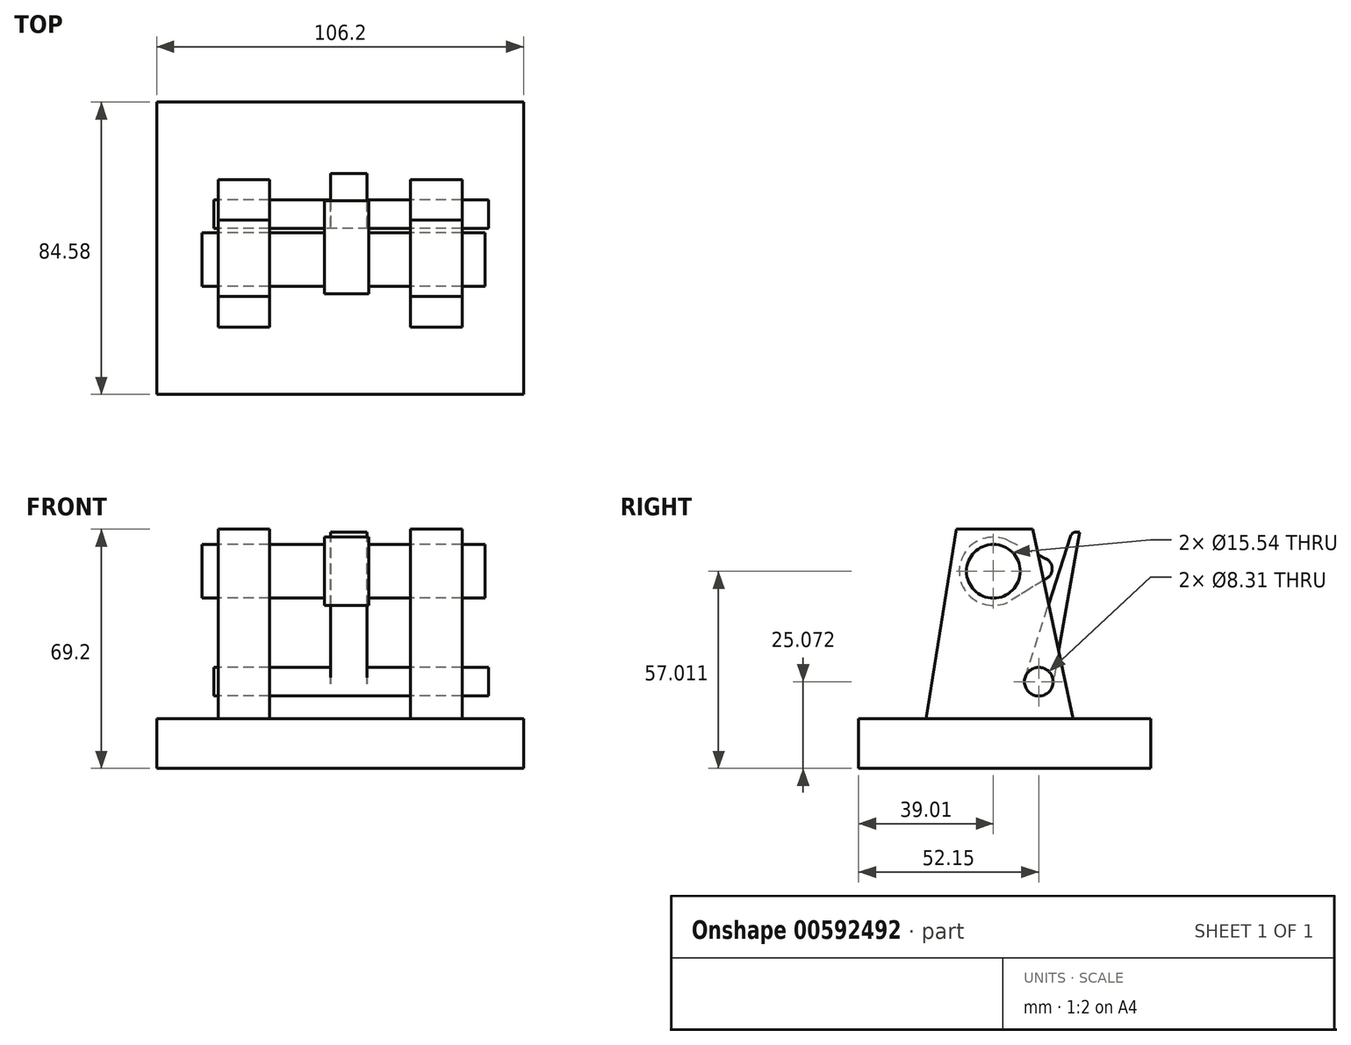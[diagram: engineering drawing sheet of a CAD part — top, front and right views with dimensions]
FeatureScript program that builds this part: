
annotation { "Feature Type Name" : "Feature", "Feature Type Description" : "" }
export const myFeature = defineFeature(function(context is Context, id is Id, definition is map)
    precondition{}
    {
        {
            var Q0;
            Q0=qCreatedBy(makeId("Right.planeOp"),FACE);
            var sketch = newSketch(context, id + "F0", { "sketchPlane" : qUnion([Q0])});
            skLineSegment(sketch, "E0.bottom", {"start": v(-39, 0) * mm, "end": v(45.57, 0) * mm});
            skLineSegment(sketch, "E0.top", {"start": v(-39, -14.35) * mm, "end": v(45.57, -14.35) * mm});
            skLineSegment(sketch, "E0.left", {"start": v(-39, 0) * mm, "end": v(-39, -14.35) * mm});
            skLineSegment(sketch, "E0.right", {"start": v(45.57, 0) * mm, "end": v(45.57, -14.35) * mm});
            skSolve(sketch);
        }
        {
            var Q0;
            Q0 = qSketchRegion(id + "F0", true);
            extrude(context, id + "F1", {"entities" : qUnion([Q0]), "endBound" : BoundingType.SYMMETRIC, "depth" : 106.2 * mm, "offsetDistance" : 25 * mm});
        }
        {
            var Q0;
            Q0=qCreatedBy(makeId("Right.planeOp"),FACE);
            var sketch = newSketch(context, id + "F2", { "sketchPlane" : qUnion([Q0])});
            skLineSegment(sketch, "E1", {"start": v(-19.5, 0) * mm, "end": v(-10.69, 54.85) * mm});
            skLineSegment(sketch, "E2", {"start": v(-10.69, 54.85) * mm, "end": v(11.44, 54.85) * mm});
            skLineSegment(sketch, "E3", {"start": v(11.44, 54.85) * mm, "end": v(23.07, 0) * mm});
            skCircle(sketch, "E4", {"center": v(0, 42.66) * mm, "radius": 7.77 * mm});
            skLineSegment(sketch, "E5.0", {"start": v(-39, 0) * mm, "end": v(45.57, 0) * mm});
            skSolve(sketch);
        }
        {
            var Q0;
            {var subQ1=sQuery(id+"F2.wireOp",EDGE,"E1");Q0=makeQuery(id+"F2.imprint","IMPRINT",FACE,{"disambiguationData":[TD([[makeQuery(id+"F2.imprint","IMPRINT",EDGE,{"derivedFrom":subQ1}),-1.0]])]});}
            extrude(context, id + "F3", {"entities" : qUnion([Q0]), "depth" : 35.3 * mm, "offsetDistance" : 25 * mm, "hasSecondDirection" : true, "secondDirectionOppositeDirection" : false, "secondDirectionDepth" : 20.4 * mm});
        }
        {
            var Q0;
            Q0=makeQuery(id+"F3.opExtrude","SWEPT_BODY",BODY,{"disambiguationData":[OSD([sQuery(id+"F2.wireOp",EDGE,"E1"),sQuery(id+"F2.wireOp",EDGE,"E2"),sQuery(id+"F2.wireOp",EDGE,"E3"),sQuery(id+"F2.wireOp",EDGE,"E4"),sQuery(id+"F2.wireOp",EDGE,"E5.0")])]});
            var Q1;
            Q1=qCreatedBy(makeId("Right.planeOp"),FACE);
            mirror(context, id + "F4", {"entities" : qUnion([Q0]), "mirrorPlane" : qUnion([Q1])});
        }
        {
            var Q0;
            Q0=makeQuery(id+"F2.imprint","IMPRINT",FACE,{"disambiguationData":[TD([[makeQuery(id+"F2.imprint","IMPRINT",EDGE,{"derivedFrom":sQuery(id+"F2.wireOp",EDGE,"E4")}),1.0]])]});
            extrude(context, id + "F5", {"entities" : qUnion([Q0]), "depth" : 42 * mm, "offsetDistance" : 25 * mm, "hasSecondDirection" : true, "secondDirectionOppositeDirection" : true, "secondDirectionDepth" : 40 * mm});
        }
        {
            var Q0;
            Q0=qCreatedBy(makeId("Right.planeOp"),FACE);
            var sketch = newSketch(context, id + "F6", { "sketchPlane" : qUnion([Q0])});
            skCircle(sketch, "E6.0.0", {"center": v(0, 42.66) * mm, "radius": 7.77 * mm});
            skArc(sketch, "E7", {"start": v(4.3, 51.57) * mm, "mid": v(-9.88, 42.15) * mm, "end": v(5.2, 34.25) * mm});
            skArc(sketch, "E8", {"start": v(15.49, 40.6) * mm, "mid": v(17.02, 43.54) * mm, "end": v(15.2, 46.3) * mm});
            skLineSegment(sketch, "E9", {"start": v(4.3, 51.57) * mm, "end": v(15.2, 46.3) * mm});
            skLineSegment(sketch, "E10", {"start": v(15.49, 40.6) * mm, "end": v(5.2, 34.25) * mm});
            skSolve(sketch);
        }
        {
            var Q0;
            Q0=makeQuery(id+"F6.imprint","IMPRINT",FACE,{"disambiguationData":[TD([[makeQuery(id+"F6.imprint","IMPRINT",EDGE,{"derivedFrom":sQuery(id+"F6.wireOp",EDGE,"E6.0.0")}),-1.0]])]});
            extrude(context, id + "F7", {"entities" : qUnion([Q0]), "operationType" : NewBodyOperationType.ADD, "depth" : 8.3 * mm, "offsetDistance" : 25 * mm, "hasSecondDirection" : true, "secondDirectionOppositeDirection" : true, "secondDirectionDepth" : 4.5 * mm});
        }
        {
            var Q0;
            {var subQ1=sQuery(id+"F2.wireOp",EDGE,"E1");Q0=makeQuery(id+"F2.imprint","IMPRINT",FACE,{"disambiguationData":[TD([[makeQuery(id+"F2.imprint","IMPRINT",EDGE,{"derivedFrom":subQ1}),-1.0]])]});}
            var sketch = newSketch(context, id + "F8", { "sketchPlane" : qUnion([Q0])});
            skCircle(sketch, "E11", {"center": v(13.14, 10.72) * mm, "radius": 4.15 * mm});
            skSolve(sketch);
        }
        {
            var Q0;
            Q0 = qSketchRegion(id + "F8", true);
            extrude(context, id + "F9", {"entities" : qUnion([Q0]), "depth" : 43 * mm, "offsetDistance" : 25 * mm, "hasSecondDirection" : true, "secondDirectionOppositeDirection" : true, "secondDirectionDepth" : 36.5 * mm});
        }
        {
            var Q0;
            Q0=makeQuery(id+"F9.opExtrude","SWEPT_BODY",BODY,{"disambiguationData":[OSD([sQuery(id+"F8.wireOp",EDGE,"E11")])]});
            var Q1;
            Q1=makeQuery(id+"F3.opExtrude","SWEPT_BODY",BODY,{"disambiguationData":[OSD([sQuery(id+"F2.wireOp",EDGE,"E1"),sQuery(id+"F2.wireOp",EDGE,"E2"),sQuery(id+"F2.wireOp",EDGE,"E3"),sQuery(id+"F2.wireOp",EDGE,"E4"),sQuery(id+"F2.wireOp",EDGE,"E5.0")])]});
            var Q2;
            Q2=makeQuery(id+"F4.opPattern","COPY",BODY,{"derivedFrom":makeQuery(id+"F3.opExtrude","SWEPT_BODY",BODY,{"disambiguationData":[OSD([sQuery(id+"F2.wireOp",EDGE,"E1"),sQuery(id+"F2.wireOp",EDGE,"E2"),sQuery(id+"F2.wireOp",EDGE,"E3"),sQuery(id+"F2.wireOp",EDGE,"E4"),sQuery(id+"F2.wireOp",EDGE,"E5.0")])]}),"instanceName":"1"});
            booleanBodies(context, id + "F10", {"operationType" : BooleanOperationType.SUBTRACTION, "tools" : qUnion([Q0]), "targets" : qUnion([Q1, Q2]), "keepTools" : true});
        }
        {
            var Q0;
            {var subQ1=sQuery(id+"F2.wireOp",EDGE,"E1");Q0=makeQuery(id+"F2.imprint","IMPRINT",FACE,{"disambiguationData":[TD([[makeQuery(id+"F2.imprint","IMPRINT",EDGE,{"derivedFrom":subQ1}),-1.0]])]});}
            var sketch = newSketch(context, id + "F11", { "sketchPlane" : qUnion([Q0])});
            skCircle(sketch, "E12.0", {"center": v(13.14, 10.72) * mm, "radius": 4.15 * mm});
            skArc(sketch, "E13.0", {"start": v(15.49, 40.6) * mm, "mid": v(17.02, 43.54) * mm, "end": v(15.2, 46.3) * mm});
            skLineSegment(sketch, "E14", {"start": v(9.19, 12) * mm, "end": v(22.3, 52.77) * mm});
            skLineSegment(sketch, "E15", {"start": v(24.07, 54.05) * mm, "end": v(24.93, 54.05) * mm});
            skLineSegment(sketch, "E16", {"start": v(24.93, 54.05) * mm, "end": v(17.23, 10) * mm});
            skPoint(sketch, "E17.visualSharp", {"position": v(22.72, 54.05) * mm});
            skArc(sketch, "E17.filletArc", {"start": v(24.07, 54.05) * mm, "mid": v(22.98, 53.7) * mm, "end": v(22.3, 52.77) * mm});
            skSolve(sketch);
        }
        {
            var Q0;
            {var subQ2=sQuery(id+"F11.wireOp",EDGE,"E15");Q0=makeQuery(id+"F11.imprint","IMPRINT",FACE,{"disambiguationData":[TD([[makeQuery(id+"F11.imprint","IMPRINT",EDGE,{"derivedFrom":subQ2}),-1.0]])]});}
            var Q1;
            {var subQ0=sQuery(id+"F11.wireOp",EDGE,"E14");var subQ1=sQuery(id+"F11.wireOp",EDGE,"E12.0");var subQ2=makeQuery(id+"F11.imprint","INTERSECT",VERTEX,{"derivedFrom":[subQ1,subQ0]});Q1=makeQuery(id+"F11.imprint","IMPRINT",FACE,{"disambiguationData":[TD([[makeQuery(id+"F11.imprint","IMPRINT",EDGE,{"disambiguationData":[TD([[subQ2,1.0]])],"derivedFrom":subQ1}),-1.0]])]});}
            extrude(context, id + "F12", {"entities" : qUnion([Q0, Q1]), "operationType" : NewBodyOperationType.ADD, "depth" : 7.8 * mm, "offsetDistance" : 25 * mm, "hasSecondDirection" : true, "secondDirectionOppositeDirection" : true, "secondDirectionDepth" : 2.8 * mm});
        }
    });
